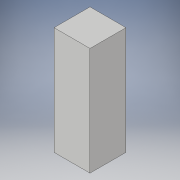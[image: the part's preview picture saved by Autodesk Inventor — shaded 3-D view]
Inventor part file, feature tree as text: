
AUTODESK INVENTOR PART (.ipt)
format: ipt  version: 2017 (Build 210142000, 142)  size: 109,056 bytes
history: native  units: in
note: dims shown in document units (in); Inventor stores cm internally (conversion verified against a paired STEP export)
features: extrude x2, sketch x1, projected_geometry x1
ambient origin geometry x8: Origin, YZ Plane, XZ Plane, XY Plane, X Axis, Y Axis, Z Axis, Center Point
bodies: Solid1 (feature_tree)
feature tree (4):
  extrude  "Extrusion1"  Depth=0.75in
  extrude  "Extrusion2"  Depth=0.25in
  sketch  "Sketch1"  dims[d6=0.25in d8=0.75in d9=0.25in d10=0.25in d11=0.25in d12=0.25in d13=0.0in d14=0.375in d16=0.25in d17=0.125in d18=0.0in d21=0.25in d22=1.25in d23=1.25in]
  projected_geometry  "Projected Loop1"
